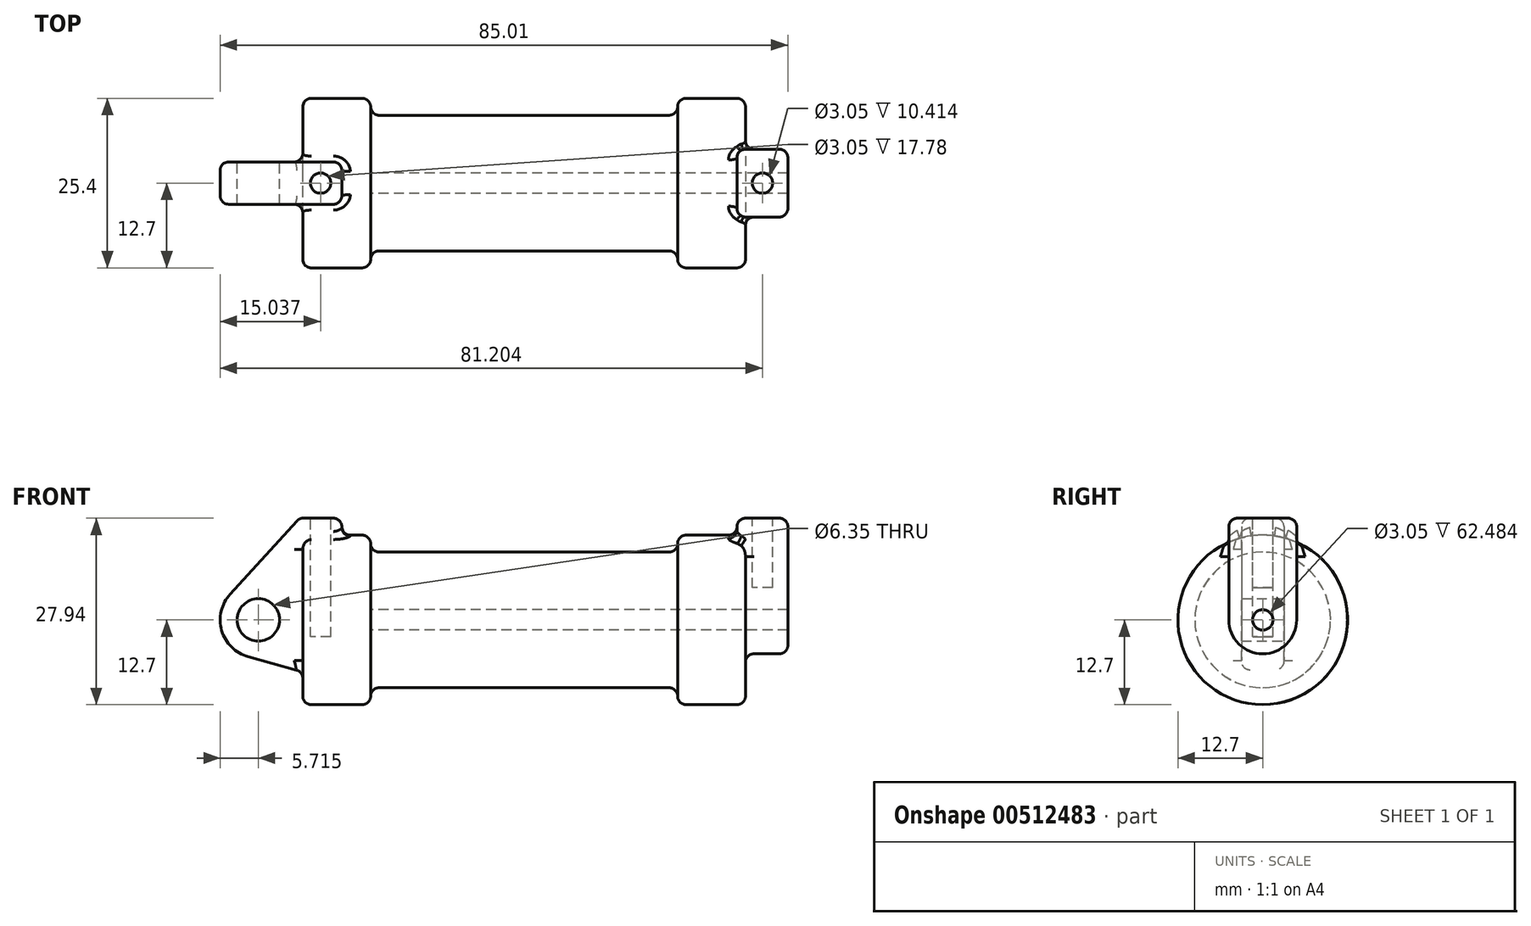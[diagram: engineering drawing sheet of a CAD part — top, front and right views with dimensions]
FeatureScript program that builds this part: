
annotation { "Feature Type Name" : "Feature", "Feature Type Description" : "" }
export const myFeature = defineFeature(function(context is Context, id is Id, definition is map)
    precondition{}
    {
        {
            var Q0;
            Q0=qCreatedBy(makeId("Front.planeOp"),FACE);
            var sketch = newSketch(context, id + "F0", { "sketchPlane" : qUnion([Q0])});
            skLineSegment(sketch, "E0", {"start": v(0, 0) * mm, "end": v(0, 12.7) * mm});
            skLineSegment(sketch, "E1", {"start": v(0, 12.7) * mm, "end": v(10.16, 12.7) * mm});
            skLineSegment(sketch, "E2", {"start": v(10.16, 12.7) * mm, "end": v(10.16, 10.16) * mm});
            skLineSegment(sketch, "E3", {"start": v(10.16, 10.16) * mm, "end": v(56.13, 10.16) * mm});
            skLineSegment(sketch, "E4", {"start": v(56.13, 10.16) * mm, "end": v(56.13, 12.7) * mm});
            skLineSegment(sketch, "E5", {"start": v(56.13, 12.7) * mm, "end": v(66.3, 12.7) * mm});
            skLineSegment(sketch, "E6", {"start": v(66.3, 12.7) * mm, "end": v(66.3, 0) * mm});
            skLineSegment(sketch, "E7", {"start": v(66.3, 0) * mm, "end": v(0, 0) * mm});
            skLineSegment(sketch, "E8", {"start": v(5.84, 15.24) * mm, "end": v(-0.5, 15.24) * mm});
            skLineSegment(sketch, "E9", {"start": v(-0.5, 15.24) * mm, "end": v(-10.88, 3.85) * mm});
            skLineSegment(sketch, "E10", {"start": v(0, 0) * mm, "end": v(-6.65, 0) * mm});
            skCircle(sketch, "E11", {"center": v(-6.65, 0) * mm, "radius": 5.72 * mm});
            skCircle(sketch, "E12", {"center": v(-6.65, 0) * mm, "radius": 3.18 * mm});
            skLineSegment(sketch, "E13", {"start": v(5.84, 15.24) * mm, "end": v(5.84, -9.4) * mm});
            skLineSegment(sketch, "E14", {"start": v(5.84, -9.4) * mm, "end": v(-8.18, -5.5) * mm});
            skSolve(sketch);
        }
        {
            var Q0;
            {var subQ0=sQuery(id+"F0.wireOp",EDGE,"E0");Q0=makeQuery(id+"F0.imprint","IMPRINT",FACE,{"disambiguationData":[TD([[makeQuery(id+"F0.imprint","IMPRINT",EDGE,{"derivedFrom":subQ0}),-1.0]])]});}
            var Q1;
            {var subQ0=sQuery(id+"F0.wireOp",EDGE,"E2");Q1=makeQuery(id+"F0.imprint","IMPRINT",FACE,{"disambiguationData":[TD([[makeQuery(id+"F0.imprint","IMPRINT",EDGE,{"derivedFrom":subQ0}),-1.0]])]});}
            var Q2;
            Q2=sQuery(id+"F0.wireOp",EDGE,"E7");
            revolve(context, id + "F1", {"entities" : qUnion([Q0, Q1]), "axis" : qUnion([Q2]), "revolveType" : RevolveType.FULL});
        }
        {
            var Q0;
            {var subQ1=sQuery(id+"F0.wireOp",EDGE,"E0");Q0=makeQuery(id+"F0.imprint","IMPRINT",FACE,{"disambiguationData":[TD([[makeQuery(id+"F0.imprint","IMPRINT",EDGE,{"derivedFrom":subQ1}),1.0]])]});}
            var Q1;
            {var subQ5=sQuery(id+"F0.wireOp",EDGE,"E12");Q1=makeQuery(id+"F0.imprint","IMPRINT",FACE,{"disambiguationData":[TD([[makeQuery(id+"F0.imprint","IMPRINT",EDGE,{"derivedFrom":subQ5}),-1.0]])]});}
            var Q2;
            {var subQ0=sQuery(id+"F0.wireOp",EDGE,"E14");Q2=makeQuery(id+"F0.imprint","IMPRINT",FACE,{"disambiguationData":[TD([[makeQuery(id+"F0.imprint","IMPRINT",EDGE,{"derivedFrom":subQ0}),-1.0]])]});}
            var Q3;
            {var subQ0=sQuery(id+"F0.wireOp",EDGE,"E0");Q3=makeQuery(id+"F0.imprint","IMPRINT",FACE,{"disambiguationData":[TD([[makeQuery(id+"F0.imprint","IMPRINT",EDGE,{"derivedFrom":subQ0}),-1.0]])]});}
            extrude(context, id + "F2", {"entities" : qUnion([Q0, Q1, Q2, Q3]), "operationType" : NewBodyOperationType.ADD, "endBound" : BoundingType.SYMMETRIC, "depth" : 6.35 * mm});
        }
        {
            var Q0;
            Q0=makeQuery(id+"F1.opRevolve","SWEPT_FACE",FACE,{"disambiguationData":[OSD([sQuery(id+"F0.wireOp",EDGE,"E6")])]});
            var sketch = newSketch(context, id + "F3", { "sketchPlane" : qUnion([Q0])});
            skCircle(sketch, "E15", {"center": v(0, 0) * mm, "radius": 1.52 * mm});
            skCircle(sketch, "E16", {"center": v(0, 0) * mm, "radius": 5.08 * mm});
            skArc(sketch, "E17.0.0", {"start": v(-3.17, 12.3) * mm, "mid": v(0, 12.7) * mm, "end": v(3.17, 12.3) * mm});
            skLineSegment(sketch, "E17.0.1", {"start": v(3.18, 12.3) * mm, "end": v(3.18, 15.24) * mm});
            skLineSegment(sketch, "E17.0.2", {"start": v(3.17, 15.24) * mm, "end": v(-3.18, 15.24) * mm});
            skLineSegment(sketch, "E17.0.3", {"start": v(-3.18, 15.24) * mm, "end": v(-3.18, 12.3) * mm});
            skLineSegment(sketch, "E18", {"start": v(-5.08, 0) * mm, "end": v(-5.08, 15.24) * mm});
            skLineSegment(sketch, "E19", {"start": v(5.08, 0) * mm, "end": v(5.08, 15.24) * mm});
            skLineSegment(sketch, "E20", {"start": v(-5.08, 15.24) * mm, "end": v(5.08, 15.24) * mm});
            skSolve(sketch);
        }
        {
            var Q0;
            {var subQ5=sQuery(id+"F3.wireOp",EDGE,"E17.0.0");Q0=makeQuery(id+"F3.imprint","IMPRINT",FACE,{"disambiguationData":[TD([[makeQuery(id+"F3.imprint","IMPRINT",EDGE,{"derivedFrom":subQ5}),1.0]])]});}
            var Q1;
            {var subQ0=sQuery(id+"F3.wireOp",EDGE,"E17.0.3");Q1=makeQuery(id+"F3.imprint","IMPRINT",FACE,{"disambiguationData":[TD([[makeQuery(id+"F3.imprint","IMPRINT",EDGE,{"derivedFrom":subQ0}),-1.0]])]});}
            var Q2;
            {var subQ0=sQuery(id+"F3.wireOp",EDGE,"E17.0.1");Q2=makeQuery(id+"F3.imprint","IMPRINT",FACE,{"disambiguationData":[TD([[makeQuery(id+"F3.imprint","IMPRINT",EDGE,{"derivedFrom":subQ0}),-1.0]])]});}
            var Q3;
            Q3=makeQuery(id+"F3.imprint","IMPRINT",FACE,{"disambiguationData":[TD([[makeQuery(id+"F3.imprint","IMPRINT",EDGE,{"derivedFrom":sQuery(id+"F3.wireOp",EDGE,"E15")}),-1.0]])]});
            var Q4;
            Q4=makeQuery(id+"F3.imprint","IMPRINT",FACE,{"disambiguationData":[TD([[makeQuery(id+"F3.imprint","IMPRINT",EDGE,{"derivedFrom":sQuery(id+"F3.wireOp",EDGE,"E17.0.0")}),-1.0]])]});
            extrude(context, id + "F4", {"entities" : qUnion([Q0, Q1, Q2, Q3, Q4]), "operationType" : NewBodyOperationType.ADD, "depth" : 6.35 * mm, "hasSecondDirection" : true, "secondDirectionOppositeDirection" : true, "secondDirectionDepth" : 1.27 * mm});
        }
        {
            var Q0;
            Q0=makeQuery(id+"F4.boolean.opBoolean","SPLIT",FACE,{"disambiguationData":[TD([makeQuery(id+"F4.opExtrude","SWEPT_FACE",FACE,{"disambiguationData":[OSD([sQuery(id+"F3.wireOp",EDGE,"E15")])]})])],"derivedFrom":makeQuery(id+"F1.opRevolve","SWEPT_FACE",FACE,{"disambiguationData":[OSD([sQuery(id+"F0.wireOp",EDGE,"E6")])]})});
            var Q1;
            Q1=makeQuery(id+"F1.opRevolve","SWEPT_FACE",FACE,{"disambiguationData":[OSD([sQuery(id+"F0.wireOp",EDGE,"E2")])]});
            extrude(context, id + "F5", {"entities" : qUnion([Q0]), "operationType" : NewBodyOperationType.REMOVE, "endBound" : BoundingType.UP_TO_SURFACE, "oppositeDirection" : true, "endBoundEntityFace" : qUnion([Q1]), "depth" : 25.4 * mm});
        }
        {
            var Q0;
            {var subQ0=sQuery(id+"F3.wireOp",EDGE,"E20");var subQ1=makeQuery(id+"F3.imprint","INTERSECT",VERTEX,{"derivedFrom":[sQuery(id+"F3.wireOp",EDGE,"E17.0.1"),subQ0]});var subQ2=makeQuery(id+"F3.imprint","INTERSECT",VERTEX,{"derivedFrom":[sQuery(id+"F3.wireOp",EDGE,"E17.0.3"),subQ0]});Q0=makeQuery(id+"F908H12IY1POlAq_1.boolean.opBoolean","MERGE",FACE,{"derivedFrom":[makeQuery(id+"F4.opExtrude","SWEPT_FACE",FACE,{"disambiguationData":[OSD([subQ0])]}),makeQuery(id+"F908H12IY1POlAq_1.opExtrude","SWEPT_FACE",FACE,{"disambiguationData":[OSD([subQ0]),TDD([makeQuery(id+"F3.imprint","IMPRINT",EDGE,{"disambiguationData":[TD([[subQ2,1.0]])],"derivedFrom":subQ0}),makeQuery(id+"F3.imprint","IMPRINT",EDGE,{"disambiguationData":[TD([[subQ1,1.0]])],"derivedFrom":subQ0}),makeQuery(id+"F3.imprint","IMPRINT",EDGE,{"disambiguationData":[TD([[subQ1,-1.0]])],"derivedFrom":subQ0})])]})]});}
            var sketch = newSketch(context, id + "F6", { "sketchPlane" : qUnion([Q0])});
            skLineSegment(sketch, "E21", {"start": v(68.83, -5.08) * mm, "end": v(68.83, 5.08) * mm, "construction": true});
            skLineSegment(sketch, "E22.0", {"start": v(66.3, 0) * mm, "end": v(0, 0) * mm});
            skCircle(sketch, "E23", {"center": v(68.83, 0) * mm, "radius": 1.52 * mm});
            skSolve(sketch);
        }
        {
            var Q0;
            Q0=makeQuery(id+"F6.imprint","IMPRINT",FACE,{"disambiguationData":[TD([[makeQuery(id+"F6.imprint","IMPRINT",EDGE,{"derivedFrom":sQuery(id+"F6.wireOp",EDGE,"E23")}),1.0]])]});
            extrude(context, id + "F7", {"entities" : qUnion([Q0]), "operationType" : NewBodyOperationType.REMOVE, "oppositeDirection" : true, "depth" : 10.4 * mm});
        }
        {
            var Q0;
            Q0=makeQuery(id+"F2.opExtrude","SWEPT_FACE",FACE,{"disambiguationData":[OSD([sQuery(id+"F0.wireOp",EDGE,"E8")])]});
            var sketch = newSketch(context, id + "F8", { "sketchPlane" : qUnion([Q0])});
            skLineSegment(sketch, "E24.0", {"start": v(66.3, 0) * mm, "end": v(0, 0) * mm});
            skLineSegment(sketch, "E25", {"start": v(2.67, 3.18) * mm, "end": v(2.67, -3.18) * mm, "construction": true});
            skCircle(sketch, "E26", {"center": v(2.67, 0) * mm, "radius": 1.52 * mm});
            skSolve(sketch);
        }
        {
            var Q0;
            {var subQ0=sQuery(id+"F8.wireOp",EDGE,"E26");var subQ1=sQuery(id+"F8.wireOp",EDGE,"E24.0");var subQ2=makeQuery(id+"F8.imprint","INTERSECT",VERTEX,{"disambiguationData":[OD(0.0)],"derivedFrom":[subQ1,subQ0]});Q0=makeQuery(id+"F8.imprint","IMPRINT",FACE,{"disambiguationData":[TD([[makeQuery(id+"F8.imprint","IMPRINT",EDGE,{"disambiguationData":[TD([[subQ2,1.0]])],"derivedFrom":subQ1}),-1.0]])]});}
            var Q1;
            {var subQ0=sQuery(id+"F8.wireOp",EDGE,"E26");var subQ1=sQuery(id+"F8.wireOp",EDGE,"E24.0");var subQ2=makeQuery(id+"F8.imprint","INTERSECT",VERTEX,{"disambiguationData":[OD(0.0)],"derivedFrom":[subQ1,subQ0]});Q1=makeQuery(id+"F8.imprint","IMPRINT",FACE,{"disambiguationData":[TD([[makeQuery(id+"F8.imprint","IMPRINT",EDGE,{"disambiguationData":[TD([[subQ2,1.0]])],"derivedFrom":subQ1}),1.0]])]});}
            extrude(context, id + "F9", {"entities" : qUnion([Q0, Q1]), "operationType" : NewBodyOperationType.REMOVE, "oppositeDirection" : true, "depth" : 17.78 * mm});
        }
        {
            var Q0;
            Q0=makeQuery(id+"F1.opRevolve","SWEPT_EDGE",EDGE,{"disambiguationData":[OSD([sQuery(id+"F0.wireOp",EDGE,"E1"),sQuery(id+"F0.wireOp",EDGE,"E2")])]});
            var Q1;
            Q1=makeQuery(id+"F1.opRevolve","SWEPT_EDGE",EDGE,{"disambiguationData":[OSD([sQuery(id+"F0.wireOp",EDGE,"E0"),sQuery(id+"F0.wireOp",EDGE,"E1")])]});
            var Q2;
            Q2=makeQuery(id+"F1.opRevolve","SWEPT_EDGE",EDGE,{"disambiguationData":[OSD([sQuery(id+"F0.wireOp",EDGE,"E4"),sQuery(id+"F0.wireOp",EDGE,"E5")])]});
            var Q3;
            {var subQ0=sQuery(id+"F0.wireOp",EDGE,"E5");var subQ1=sQuery(id+"F0.wireOp",EDGE,"E6");Q3=makeQuery(id+"F4.boolean.opBoolean","SPLIT",EDGE,{"disambiguationData":[topologyDisambiguationEdgeConnected([makeQuery(id+"F1.opRevolve","SWEPT_FACE",FACE,{"disambiguationData":[OSD([subQ1])]})])],"derivedFrom":makeQuery(id+"F1.opRevolve","SWEPT_EDGE",EDGE,{"disambiguationData":[OSD([subQ0,subQ1])]})});}
            fillet(context, id + "F10", {"entities" : qUnion([Q0, Q1, Q2, Q3]), "radius" : 1.27 * mm, "tangentPropagation" : true, "allowEdgeOverflow" : false});
        }
        {
            var Q0;
            Q0=makeQuery(id+"F1.opRevolve","SWEPT_FACE",FACE,{"disambiguationData":[OSD([sQuery(id+"F0.wireOp",EDGE,"E0")])]});
            var Q1;
            Q1=makeQuery(id+"F2.opExtrude","SWEPT_FACE",FACE,{"disambiguationData":[OSD([sQuery(id+"F0.wireOp",EDGE,"E9")])]});
            var Q2;
            Q2=makeQuery(id+"F2.opExtrude","CAP_EDGE",EDGE,{"disambiguationData":[OSD([sQuery(id+"F0.wireOp",EDGE,"E8")])],"isStart":false});
            var Q3;
            Q3=makeQuery(id+"F2.opExtrude","CAP_EDGE",EDGE,{"disambiguationData":[OSD([sQuery(id+"F0.wireOp",EDGE,"E8")])],"isStart":true});
            var Q4;
            Q4=makeQuery(id+"F2.opExtrude","SWEPT_FACE",FACE,{"disambiguationData":[OSD([sQuery(id+"F0.wireOp",EDGE,"E13")])]});
            fillet(context, id + "F11", {"entities" : qUnion([Q0, Q1, Q2, Q3, Q4]), "radius" : 1.27 * mm, "tangentPropagation" : true, "allowEdgeOverflow" : false});
        }
        {
            var Q0;
            Q0=makeQuery(id+"F1.opRevolve","SWEPT_EDGE",EDGE,{"disambiguationData":[OSD([sQuery(id+"F0.wireOp",EDGE,"E3"),sQuery(id+"F0.wireOp",EDGE,"E4")])]});
            var Q1;
            Q1=makeQuery(id+"F1.opRevolve","SWEPT_EDGE",EDGE,{"disambiguationData":[OSD([sQuery(id+"F0.wireOp",EDGE,"E2"),sQuery(id+"F0.wireOp",EDGE,"E3")])]});
            fillet(context, id + "F12", {"entities" : qUnion([Q0, Q1]), "radius" : 1.27 * mm, "tangentPropagation" : true, "allowEdgeOverflow" : false});
        }
        {
            var Q0;
            Q0=makeQuery(id+"F4.opExtrude","SWEPT_FACE",FACE,{"disambiguationData":[OSD([sQuery(id+"F3.wireOp",EDGE,"E18")])]});
            var Q1;
            Q1=makeQuery(id+"F4.opExtrude","SWEPT_FACE",FACE,{"disambiguationData":[OSD([sQuery(id+"F3.wireOp",EDGE,"E19")])]});
            var Q2;
            Q2=makeQuery(id+"F4.opExtrude","SWEPT_FACE",FACE,{"disambiguationData":[OSD([sQuery(id+"F3.wireOp",EDGE,"E16")])]});
            var Q3;
            Q3=makeQuery(id+"F4.opExtrude","CAP_EDGE",EDGE,{"disambiguationData":[OSD([sQuery(id+"F3.wireOp",EDGE,"E20")])],"isStart":false});
            var Q4;
            Q4=makeQuery(id+"F4.opExtrude","CAP_FACE",FACE,{"disambiguationData":[OSD([sQuery(id+"F3.wireOp",EDGE,"E15"),sQuery(id+"F3.wireOp",EDGE,"E16"),sQuery(id+"F3.wireOp",EDGE,"E18"),sQuery(id+"F3.wireOp",EDGE,"E19"),sQuery(id+"F3.wireOp",EDGE,"E20")])],"isStart":true});
            fillet(context, id + "F13", {"entities" : qUnion([Q0, Q1, Q2, Q3, Q4]), "radius" : 1.27 * mm, "tangentPropagation" : true, "allowEdgeOverflow" : false});
        }
    });
